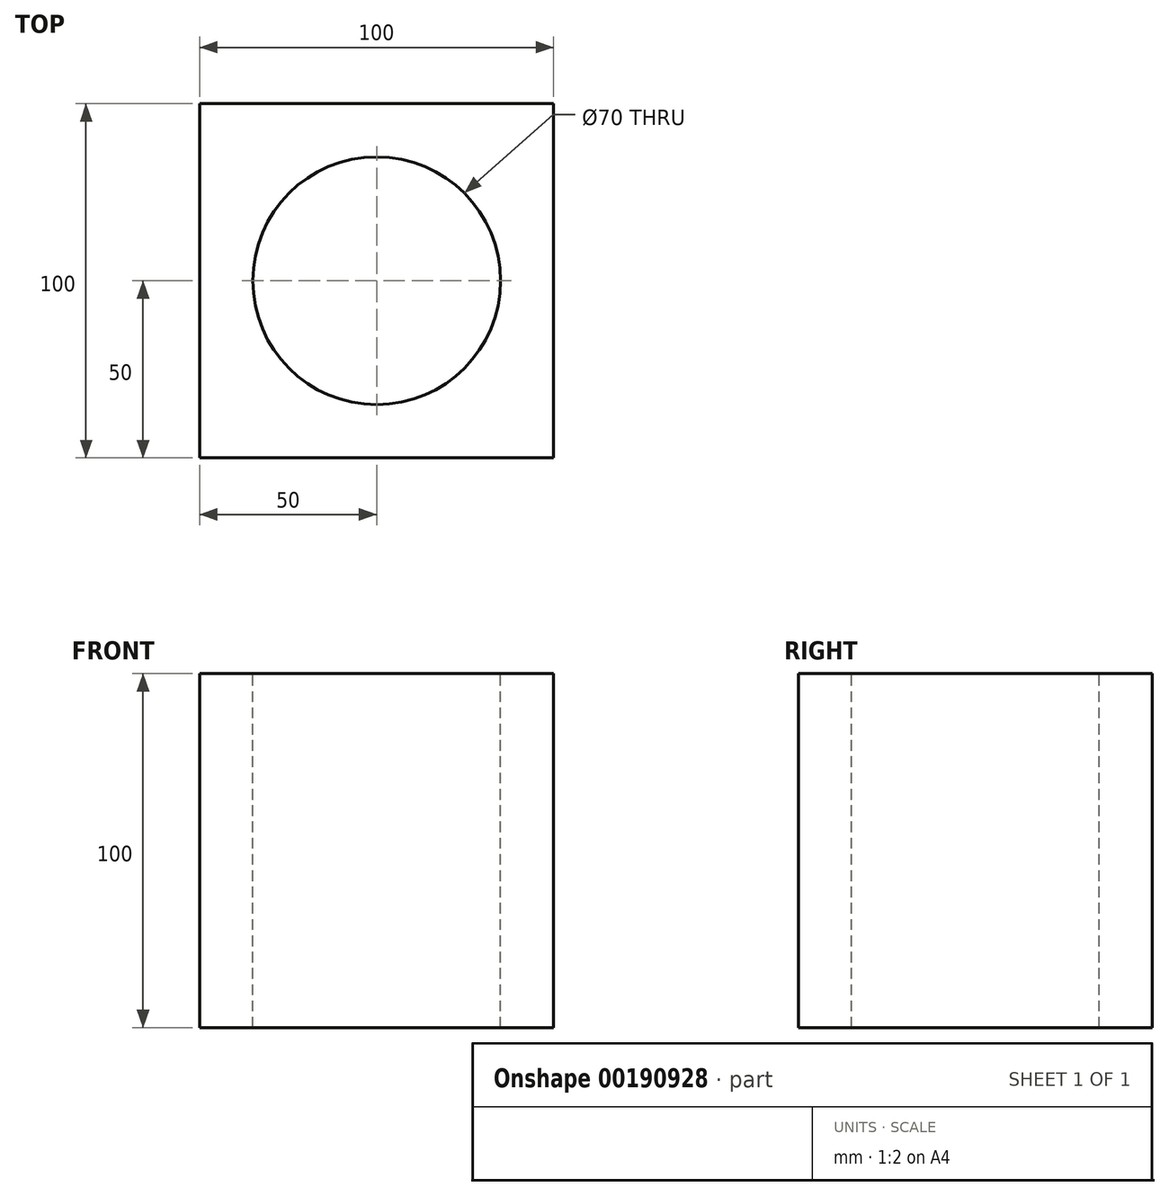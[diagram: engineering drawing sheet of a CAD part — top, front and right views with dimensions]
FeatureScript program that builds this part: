
annotation { "Feature Type Name" : "Feature", "Feature Type Description" : "" }
export const myFeature = defineFeature(function(context is Context, id is Id, definition is map)
    precondition{}
    {
        {
            var Q0;
            Q0=qCreatedBy(makeId("Top.planeOp"),FACE);
            var sketch = newSketch(context, id + "F0", { "sketchPlane" : qUnion([Q0])});
            skLineSegment(sketch, "E0.bottom", {"start": v(50, 50) * mm, "end": v(-50, 50) * mm});
            skLineSegment(sketch, "E0.top", {"start": v(50, -50) * mm, "end": v(-50, -50) * mm});
            skLineSegment(sketch, "E0.left", {"start": v(50, 50) * mm, "end": v(50, -50) * mm});
            skLineSegment(sketch, "E0.right", {"start": v(-50, 50) * mm, "end": v(-50, -50) * mm});
            skPoint(sketch, "E0.middle", {"position": v(0, 0) * mm});
            skSolve(sketch);
        }
        {
            var Q0;
            Q0 = qSketchRegion(id + "F0", true);
            extrude(context, id + "F1", {"entities" : qUnion([Q0]), "depth" : 100 * mm, "offsetDistance" : 25 * mm, "symmetric" : true});
        }
        {
            var Q0;
            Q0=qCreatedBy(makeId("Top.planeOp"),FACE);
            var sketch = newSketch(context, id + "F2", { "sketchPlane" : qUnion([Q0])});
            skCircle(sketch, "E1", {"center": v(0, 0) * mm, "radius": 35 * mm});
            skSolve(sketch);
        }
        {
            var Q0;
            Q0 = qSketchRegion(id + "F2", true);
            extrude(context, id + "F3", {"entities" : qUnion([Q0]), "operationType" : NewBodyOperationType.REMOVE, "endBound" : BoundingType.THROUGH_ALL, "oppositeDirection" : true, "depth" : 25 * mm, "offsetDistance" : 25 * mm, "hasSecondDirection" : true, "secondDirectionBound" : BoundingType.THROUGH_ALL, "secondDirectionOppositeDirection" : false, "secondDirectionDepth" : 25 * mm});
        }
        {
            var Q0;
            Q0=qCreatedBy(makeId("Top.planeOp"),FACE);
            var sketch = newSketch(context, id + "F4", { "sketchPlane" : qUnion([Q0])});
            skLineSegment(sketch, "E2", {"start": v(0, -71.57) * mm, "end": v(0, 51) * mm});
            skLineSegment(sketch, "E3", {"start": v(73.03, 0) * mm, "end": v(-56.5, 0) * mm});
            skSolve(sketch);
        }
    });
